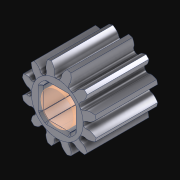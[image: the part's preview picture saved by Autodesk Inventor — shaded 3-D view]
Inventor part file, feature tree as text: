
AUTODESK INVENTOR PART (.ipt)
format: ipt  version: 2021 (Build 250183000, 183)  size: 391,168 bytes
history: native  units: in
note: dims shown in document units (in); Inventor stores cm internally (conversion verified against a paired STEP export)
features: sketch x1, other x1, extrude x1
ambient origin geometry x8: Origin, YZ Plane, XZ Plane, XY Plane, X Axis, Y Axis, Z Axis, Center Point
bodies: Solid1 (feature_tree), Body1 (feature_tree)
feature tree (3):
  sketch  "Sketch1"  dims[d0=1.0in d1=0.0in]
  other  "Srf1"
  extrude  "ExtrusionSrf1"  [1 undecoded]
note: 1 required parameter value undecoded (feature->parameter linkage not recoverable at this tier; creation-order binding heuristic only, values carry confidence <= 0.55)
